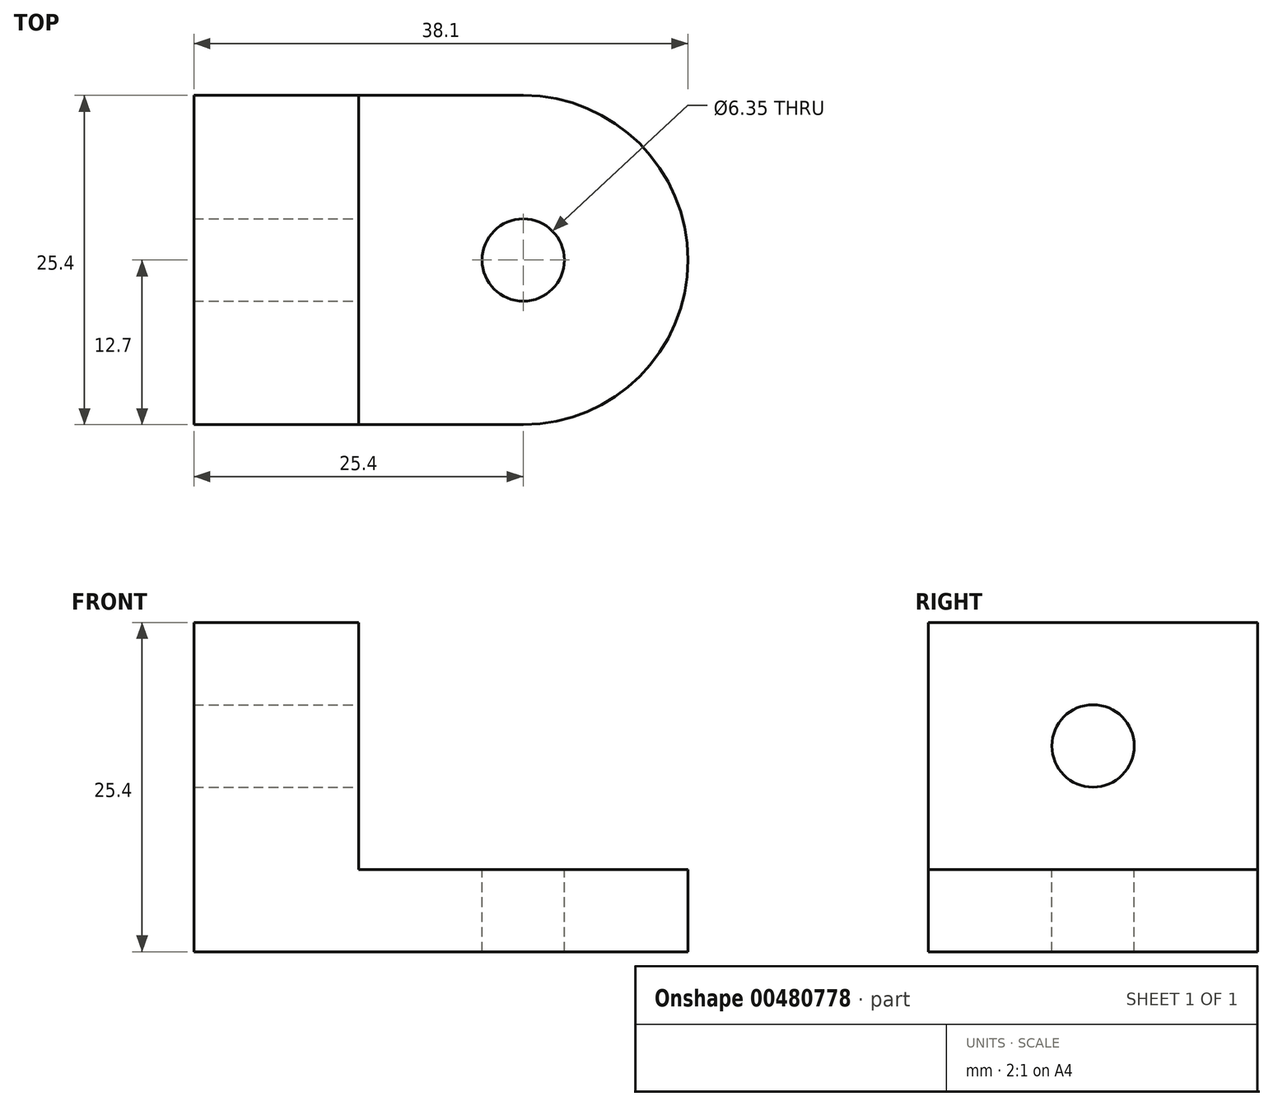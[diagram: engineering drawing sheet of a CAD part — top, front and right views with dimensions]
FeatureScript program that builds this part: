
annotation { "Feature Type Name" : "Feature", "Feature Type Description" : "" }
export const myFeature = defineFeature(function(context is Context, id is Id, definition is map)
    precondition{}
    {
        {
            var Q0;
            Q0=qCreatedBy(makeId("Top.planeOp"),FACE);
            var sketch = newSketch(context, id + "F0", { "sketchPlane" : qUnion([Q0])});
            skLineSegment(sketch, "E0", {"start": v(0, 0) * mm, "end": v(-12.7, 0) * mm});
            skLineSegment(sketch, "E1", {"start": v(-12.7, 0) * mm, "end": v(-12.7, 25.4) * mm});
            skLineSegment(sketch, "E2", {"start": v(-12.7, 25.4) * mm, "end": v(0, 25.4) * mm});
            skLineSegment(sketch, "E3", {"start": v(0, 25.4) * mm, "end": v(0, 0) * mm});
            skSolve(sketch);
        }
        {
            var Q0;
            Q0 = qSketchRegion(id + "F0", true);
            extrude(context, id + "F1", {"entities" : qUnion([Q0]), "depth" : 25.4 * mm});
        }
        {
            var Q0;
            Q0=qCreatedBy(makeId("Top.planeOp"),FACE);
            var sketch = newSketch(context, id + "F2", { "sketchPlane" : qUnion([Q0])});
            skLineSegment(sketch, "E4", {"start": v(0, 0) * mm, "end": v(12.7, 0) * mm});
            skArc(sketch, "E5", {"start": v(12.7, 0) * mm, "mid": v(25.4, 12.7) * mm, "end": v(12.7, 25.4) * mm});
            skLineSegment(sketch, "E6", {"start": v(0, 0) * mm, "end": v(0, 25.4) * mm});
            skLineSegment(sketch, "E7", {"start": v(0, 25.4) * mm, "end": v(12.7, 25.4) * mm});
            skSolve(sketch);
        }
        {
            var Q0;
            Q0 = qSketchRegion(id + "F2", true);
            extrude(context, id + "F3", {"entities" : qUnion([Q0]), "operationType" : NewBodyOperationType.ADD, "depth" : 6.35 * mm});
        }
        {
            var Q0;
            Q0=makeQuery(id+"F1.opExtrude","SWEPT_FACE",FACE,{"disambiguationData":[OSD([sQuery(id+"F0.wireOp",EDGE,"E3")])]});
            var sketch = newSketch(context, id + "F4", { "sketchPlane" : qUnion([Q0])});
            skCircle(sketch, "E8", {"center": v(12.7, 15.88) * mm, "radius": 3.18 * mm});
            skPoint(sketch, "E8.centerSnap0", {"position": v(12.7, 6.35) * mm});
            skSolve(sketch);
        }
        {
            var Q0;
            Q0=sQuery(id+"F4.wireOp",VERTEX,"E8.center");
            var Q1;
            Q1=makeQuery(id+"F1.opExtrude","SWEPT_BODY",BODY,{"disambiguationData":[OSD([sQuery(id+"F0.wireOp",EDGE,"E0"),sQuery(id+"F0.wireOp",EDGE,"E1"),sQuery(id+"F0.wireOp",EDGE,"E2"),sQuery(id+"F0.wireOp",EDGE,"E3")])]});
            hole(context, id + "F5", {"style" : HoleStyle.SIMPLE, "endStyle" : HoleEndStyle.THROUGH, "holeDiameter" : 6.35 * mm, "isTappedThrough" : true, "tappedDepth" : 12.7 * mm, "tapClearance" : 3, "locations" : qUnion([Q0]), "scope" : qUnion([Q1])});
        }
        {
            var Q0;
            Q0=makeQuery(id+"F3.opExtrude","CAP_FACE",FACE,{"disambiguationData":[OSD([sQuery(id+"F2.wireOp",EDGE,"E4"),sQuery(id+"F2.wireOp",EDGE,"E5"),sQuery(id+"F2.wireOp",EDGE,"E6"),sQuery(id+"F2.wireOp",EDGE,"E7")])],"isStart":false});
            var sketch = newSketch(context, id + "F6", { "sketchPlane" : qUnion([Q0])});
            skCircle(sketch, "E9", {"center": v(12.7, 12.7) * mm, "radius": 3.18 * mm});
            skSolve(sketch);
        }
        {
            var Q0;
            Q0=sQuery(id+"F6.wireOp",VERTEX,"E9.center");
            var Q1;
            Q1=makeQuery(id+"F1.opExtrude","SWEPT_BODY",BODY,{"disambiguationData":[OSD([sQuery(id+"F0.wireOp",EDGE,"E0"),sQuery(id+"F0.wireOp",EDGE,"E1"),sQuery(id+"F0.wireOp",EDGE,"E2"),sQuery(id+"F0.wireOp",EDGE,"E3")])]});
            hole(context, id + "F7", {"style" : HoleStyle.SIMPLE, "endStyle" : HoleEndStyle.THROUGH, "holeDiameter" : 6.35 * mm, "isTappedThrough" : true, "tappedDepth" : 12.7 * mm, "tapClearance" : 3, "locations" : qUnion([Q0]), "scope" : qUnion([Q1])});
        }
    });
